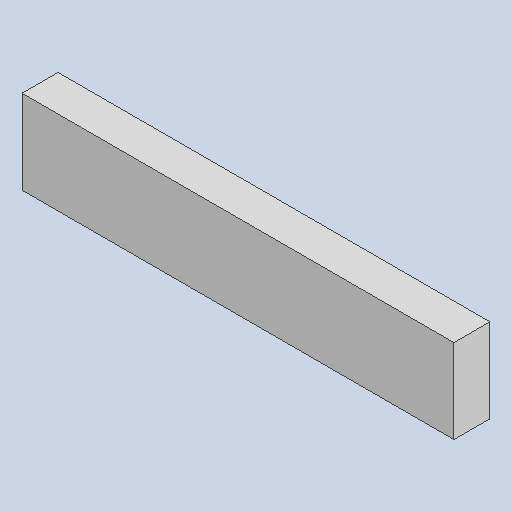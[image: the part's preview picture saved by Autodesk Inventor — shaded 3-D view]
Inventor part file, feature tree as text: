
AUTODESK INVENTOR PART (.ipt)
format: ipt  version: 2025 (Build 290162000, 162)  size: 124,416 bytes
history: native  units: in
note: dims shown in document units (in); Inventor stores cm internally (conversion verified against a paired STEP export)
features: other x4, reference x2, extrude x1, sketch x1
ambient origin geometry x8: Origin, YZ Plane, XZ Plane, XY Plane, X Axis, Y Axis, Z Axis, Center Point
bodies: Solid1 (feature_tree)
feature tree (8):
  extrude  "Extrusion1"  Depth=1.5in TaperAngle=0.0deg
  sketch  "Sketch1"  dims[d0=3.5in d1=1.5in d2=0.0in]
  reference  "Reference1"
  reference  "Reference2"
  other  "<userpath>\Documents\Tburn24\F_Legs2\F_Legs2.iam"
  other  "F_Legs2.iam"
  other  "side-side:2"
  other  "side-side:1"
